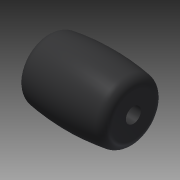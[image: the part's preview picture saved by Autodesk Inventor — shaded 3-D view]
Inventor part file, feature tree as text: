
AUTODESK INVENTOR PART (.ipt)
format: ipt  version: 2015 (Build 190159000, 159)  size: 144,896 bytes
history: native  units: in
note: dims shown in document units (in); Inventor stores cm internally (conversion verified against a paired STEP export)
features: revolve x1, other x1, imported_body x1
ambient origin geometry x8: Origin, YZ Plane, XZ Plane, XY Plane, X Axis, Y Axis, Z Axis, Center Point
bodies: Body1 (feature_tree)
feature tree (3):
  revolve  "Revolve1"  [1 undecoded]
  other  "tetrix_736466_roller1"
  imported_body  "Base1"
note: 1 required parameter value undecoded (feature->parameter linkage not recoverable at this tier; creation-order binding heuristic only, values carry confidence <= 0.55)
